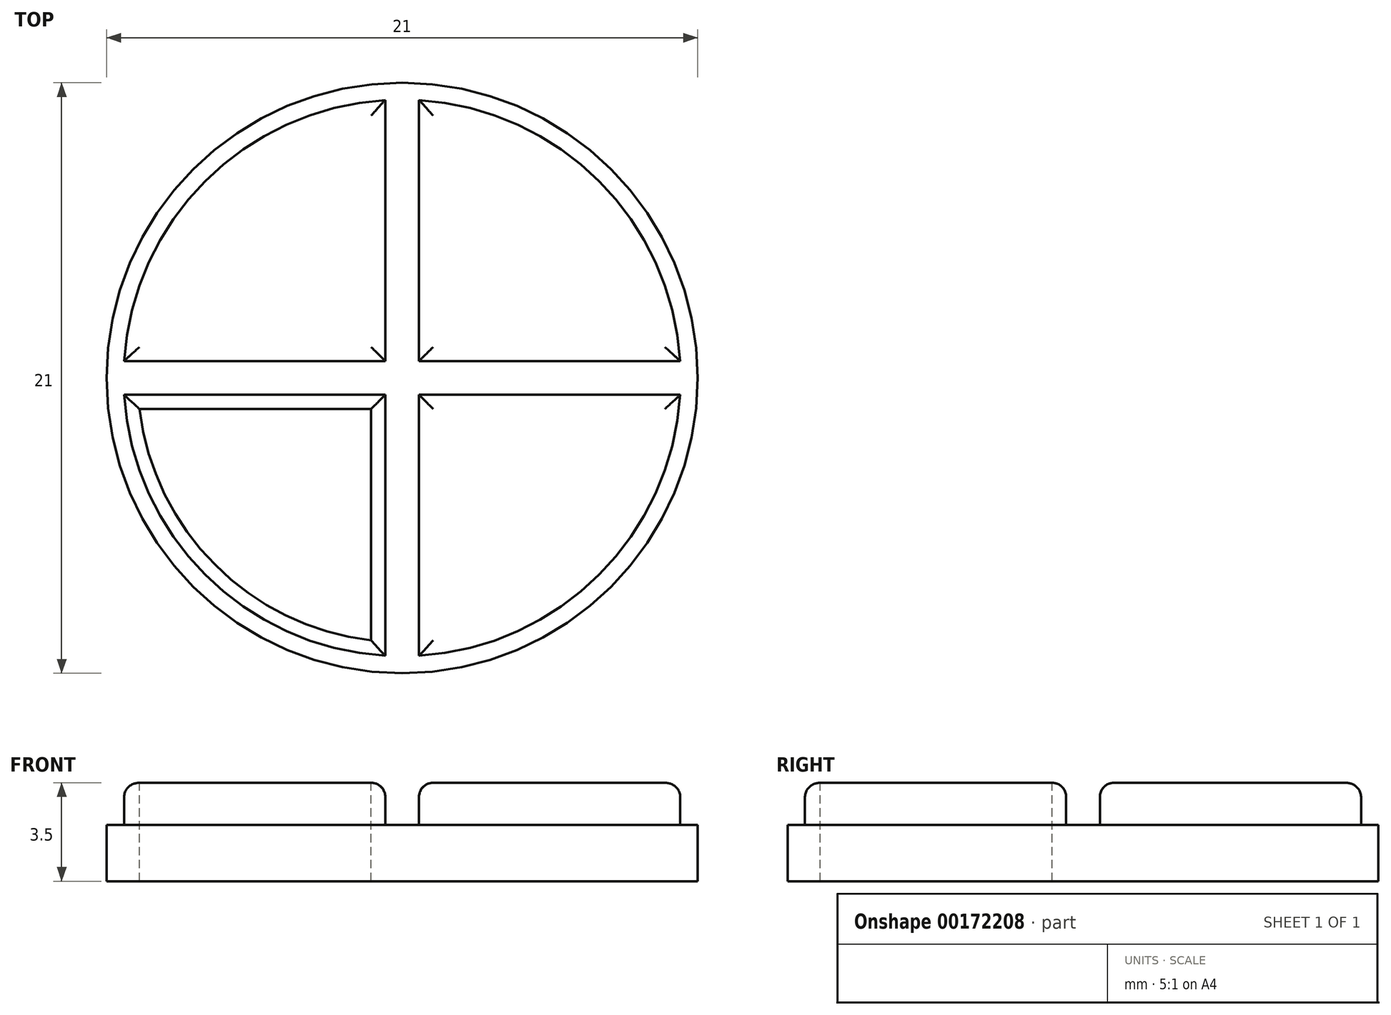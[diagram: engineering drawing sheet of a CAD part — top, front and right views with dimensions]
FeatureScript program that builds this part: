
annotation { "Feature Type Name" : "Feature", "Feature Type Description" : "" }
export const myFeature = defineFeature(function(context is Context, id is Id, definition is map)
    precondition{}
    {
        {
            var Q0;
            Q0=qCreatedBy(makeId("Top.planeOp"),FACE);
            var sketch = newSketch(context, id + "F0", { "sketchPlane" : qUnion([Q0])});
            skCircle(sketch, "E0", {"center": v(0, 0) * mm, "radius": 10.5 * mm});
            skSolve(sketch);
        }
        {
            var Q0;
            Q0=qSketchRegion(id+"F0",true);
            extrude(context, id + "F1", {"entities" : qUnion([Q0]), "depth" : 2 * mm});
        }
        {
            var Q0;
            Q0=makeQuery(id+"F1.opExtrude","CAP_FACE",FACE,{"disambiguationData":[OSD([sQuery(id+"F0.wireOp",EDGE,"E0")])],"isStart":false});
            var sketch = newSketch(context, id + "F2", { "sketchPlane" : qUnion([Q0])});
            skCircle(sketch, "E1", {"center": v(0, 0) * mm, "radius": 9.9 * mm});
            skLineSegment(sketch, "E2.bottom", {"start": v(9.88, -0.6) * mm, "end": v(-9.88, -0.6) * mm});
            skLineSegment(sketch, "E2.top", {"start": v(9.88, 0.6) * mm, "end": v(-9.88, 0.6) * mm});
            skLineSegment(sketch, "E2.left", {"start": v(9.88, -0.6) * mm, "end": v(9.88, 0.6) * mm});
            skLineSegment(sketch, "E2.right", {"start": v(-9.88, -0.6) * mm, "end": v(-9.88, 0.6) * mm});
            skLineSegment(sketch, "E3.bottom", {"start": v(0.6, -9.88) * mm, "end": v(-0.6, -9.88) * mm});
            skLineSegment(sketch, "E3.top", {"start": v(0.6, 9.88) * mm, "end": v(-0.6, 9.88) * mm});
            skLineSegment(sketch, "E3.left", {"start": v(0.6, -9.88) * mm, "end": v(0.6, 9.88) * mm});
            skLineSegment(sketch, "E3.right", {"start": v(-0.6, -9.88) * mm, "end": v(-0.6, 9.88) * mm});
            skSolve(sketch);
        }
        {
            var Q0;
            {var subQ0=sQuery(id+"F2.wireOp",EDGE,"E2.bottom");var subQ3=sQuery(id+"F2.wireOp",EDGE,"E3.right");var subQ5=makeQuery(id+"F2.imprint","INTERSECT",VERTEX,{"derivedFrom":[subQ0,subQ3]});Q0=makeQuery(id+"F2.imprint","IMPRINT",FACE,{"disambiguationData":[TD([[makeQuery(id+"F2.imprint","IMPRINT",EDGE,{"disambiguationData":[TD([[subQ5,-1.0]])],"derivedFrom":subQ0}),1.0]])]});}
            var Q1;
            {var subQ0=sQuery(id+"F2.wireOp",EDGE,"E2.top");var subQ3=sQuery(id+"F2.wireOp",EDGE,"E3.right");var subQ5=makeQuery(id+"F2.imprint","INTERSECT",VERTEX,{"derivedFrom":[subQ0,subQ3]});Q1=makeQuery(id+"F2.imprint","IMPRINT",FACE,{"disambiguationData":[TD([[makeQuery(id+"F2.imprint","IMPRINT",EDGE,{"disambiguationData":[TD([[subQ5,-1.0]])],"derivedFrom":subQ0}),-1.0]])]});}
            var Q2;
            {var subQ0=sQuery(id+"F2.wireOp",EDGE,"E2.top");var subQ3=sQuery(id+"F2.wireOp",EDGE,"E3.left");var subQ5=makeQuery(id+"F2.imprint","INTERSECT",VERTEX,{"derivedFrom":[subQ0,subQ3]});Q2=makeQuery(id+"F2.imprint","IMPRINT",FACE,{"disambiguationData":[TD([[makeQuery(id+"F2.imprint","IMPRINT",EDGE,{"disambiguationData":[TD([[subQ5,1.0]])],"derivedFrom":subQ0}),-1.0]])]});}
            var Q3;
            {var subQ0=sQuery(id+"F2.wireOp",EDGE,"E2.bottom");var subQ3=sQuery(id+"F2.wireOp",EDGE,"E3.left");var subQ5=makeQuery(id+"F2.imprint","INTERSECT",VERTEX,{"derivedFrom":[subQ0,subQ3]});Q3=makeQuery(id+"F2.imprint","IMPRINT",FACE,{"disambiguationData":[TD([[makeQuery(id+"F2.imprint","IMPRINT",EDGE,{"disambiguationData":[TD([[subQ5,1.0]])],"derivedFrom":subQ0}),1.0]])]});}
            extrude(context, id + "F3", {"entities" : qUnion([Q0, Q1, Q2, Q3]), "operationType" : NewBodyOperationType.ADD, "depth" : 1.5 * mm});
        }
        {
            var Q0;
            {var subQ0=sQuery(id+"F2.wireOp",EDGE,"E1");Q0=makeQuery(id+"F3.opExtrude","CAP_EDGE",EDGE,{"disambiguationData":[OSD([subQ0]),TDD([makeQuery(id+"F2.imprint","IMPRINT",EDGE,{"disambiguationData":[TD([[makeQuery(id+"F2.imprint","INTERSECT",VERTEX,{"derivedFrom":[subQ0,sQuery(id+"F2.wireOp",EDGE,"E2.bottom"),sQuery(id+"F2.wireOp",EDGE,"E2.right")]}),-1.0]])],"derivedFrom":subQ0})])],"isStart":false});}
            var Q1;
            {var subQ0=sQuery(id+"F2.wireOp",EDGE,"E3.right");Q1=makeQuery(id+"F3.opExtrude","CAP_EDGE",EDGE,{"disambiguationData":[OSD([subQ0]),TDD([makeQuery(id+"F2.imprint","IMPRINT",EDGE,{"disambiguationData":[TD([[makeQuery(id+"F2.imprint","INTERSECT",VERTEX,{"derivedFrom":[sQuery(id+"F2.wireOp",EDGE,"E2.bottom"),subQ0]}),1.0]])],"derivedFrom":subQ0})])],"isStart":false});}
            var Q2;
            {var subQ0=sQuery(id+"F2.wireOp",EDGE,"E2.bottom");Q2=makeQuery(id+"F3.opExtrude","CAP_EDGE",EDGE,{"disambiguationData":[OSD([subQ0]),TDD([makeQuery(id+"F2.imprint","IMPRINT",EDGE,{"disambiguationData":[TD([[makeQuery(id+"F2.imprint","INTERSECT",VERTEX,{"derivedFrom":[subQ0,sQuery(id+"F2.wireOp",EDGE,"E3.right")]}),-1.0]])],"derivedFrom":subQ0})])],"isStart":false});}
            var Q3;
            {var subQ0=sQuery(id+"F2.wireOp",EDGE,"E2.top");Q3=makeQuery(id+"F3.opExtrude","CAP_EDGE",EDGE,{"disambiguationData":[OSD([subQ0]),TDD([makeQuery(id+"F2.imprint","IMPRINT",EDGE,{"disambiguationData":[TD([[makeQuery(id+"F2.imprint","INTERSECT",VERTEX,{"derivedFrom":[subQ0,sQuery(id+"F2.wireOp",EDGE,"E3.right")]}),-1.0]])],"derivedFrom":subQ0})])],"isStart":false});}
            var Q4;
            {var subQ0=sQuery(id+"F2.wireOp",EDGE,"E3.right");Q4=makeQuery(id+"F3.opExtrude","CAP_EDGE",EDGE,{"disambiguationData":[OSD([subQ0]),TDD([makeQuery(id+"F2.imprint","IMPRINT",EDGE,{"disambiguationData":[TD([[makeQuery(id+"F2.imprint","INTERSECT",VERTEX,{"derivedFrom":[sQuery(id+"F2.wireOp",EDGE,"E2.top"),subQ0]}),-1.0]])],"derivedFrom":subQ0})])],"isStart":false});}
            var Q5;
            {var subQ0=sQuery(id+"F2.wireOp",EDGE,"E2.top");Q5=makeQuery(id+"F3.opExtrude","CAP_EDGE",EDGE,{"disambiguationData":[OSD([subQ0]),TDD([makeQuery(id+"F2.imprint","IMPRINT",EDGE,{"disambiguationData":[TD([[makeQuery(id+"F2.imprint","INTERSECT",VERTEX,{"derivedFrom":[subQ0,sQuery(id+"F2.wireOp",EDGE,"E3.left")]}),1.0]])],"derivedFrom":subQ0})])],"isStart":false});}
            var Q6;
            {var subQ0=sQuery(id+"F2.wireOp",EDGE,"E3.left");Q6=makeQuery(id+"F3.opExtrude","CAP_EDGE",EDGE,{"disambiguationData":[OSD([subQ0]),TDD([makeQuery(id+"F2.imprint","IMPRINT",EDGE,{"disambiguationData":[TD([[makeQuery(id+"F2.imprint","INTERSECT",VERTEX,{"derivedFrom":[sQuery(id+"F2.wireOp",EDGE,"E2.top"),subQ0]}),-1.0]])],"derivedFrom":subQ0})])],"isStart":false});}
            var Q7;
            {var subQ0=sQuery(id+"F2.wireOp",EDGE,"E2.bottom");Q7=makeQuery(id+"F3.opExtrude","CAP_EDGE",EDGE,{"disambiguationData":[OSD([subQ0]),TDD([makeQuery(id+"F2.imprint","IMPRINT",EDGE,{"disambiguationData":[TD([[makeQuery(id+"F2.imprint","INTERSECT",VERTEX,{"derivedFrom":[subQ0,sQuery(id+"F2.wireOp",EDGE,"E3.left")]}),1.0]])],"derivedFrom":subQ0})])],"isStart":false});}
            var Q8;
            {var subQ0=sQuery(id+"F2.wireOp",EDGE,"E3.left");Q8=makeQuery(id+"F3.opExtrude","CAP_EDGE",EDGE,{"disambiguationData":[OSD([subQ0]),TDD([makeQuery(id+"F2.imprint","IMPRINT",EDGE,{"disambiguationData":[TD([[makeQuery(id+"F2.imprint","INTERSECT",VERTEX,{"derivedFrom":[sQuery(id+"F2.wireOp",EDGE,"E2.bottom"),subQ0]}),1.0]])],"derivedFrom":subQ0})])],"isStart":false});}
            var Q9;
            {var subQ0=sQuery(id+"F2.wireOp",EDGE,"E1");Q9=makeQuery(id+"F3.opExtrude","CAP_EDGE",EDGE,{"disambiguationData":[OSD([subQ0]),TDD([makeQuery(id+"F2.imprint","IMPRINT",EDGE,{"disambiguationData":[TD([[makeQuery(id+"F2.imprint","INTERSECT",VERTEX,{"derivedFrom":[subQ0,sQuery(id+"F2.wireOp",EDGE,"E2.bottom"),sQuery(id+"F2.wireOp",EDGE,"E2.left")]}),1.0]])],"derivedFrom":subQ0})])],"isStart":false});}
            var Q10;
            {var subQ0=sQuery(id+"F2.wireOp",EDGE,"E1");Q10=makeQuery(id+"F3.opExtrude","CAP_EDGE",EDGE,{"disambiguationData":[OSD([subQ0]),TDD([makeQuery(id+"F2.imprint","IMPRINT",EDGE,{"disambiguationData":[TD([[makeQuery(id+"F2.imprint","INTERSECT",VERTEX,{"derivedFrom":[subQ0,sQuery(id+"F2.wireOp",EDGE,"E2.top"),sQuery(id+"F2.wireOp",EDGE,"E2.left")]}),-1.0]])],"derivedFrom":subQ0})])],"isStart":false});}
            var Q11;
            {var subQ0=sQuery(id+"F2.wireOp",EDGE,"E1");Q11=makeQuery(id+"F3.opExtrude","CAP_EDGE",EDGE,{"disambiguationData":[OSD([subQ0]),TDD([makeQuery(id+"F2.imprint","IMPRINT",EDGE,{"disambiguationData":[TD([[makeQuery(id+"F2.imprint","INTERSECT",VERTEX,{"derivedFrom":[subQ0,sQuery(id+"F2.wireOp",EDGE,"E2.top"),sQuery(id+"F2.wireOp",EDGE,"E2.right")]}),1.0]])],"derivedFrom":subQ0})])],"isStart":false});}
            fillet(context, id + "F4", {"entities" : qUnion([Q0, Q1, Q2, Q3, Q4, Q5, Q6, Q7, Q8, Q9, Q10, Q11]), "radius" : 0.5 * mm, "tangentPropagation" : true, "allowEdgeOverflow" : false});
        }
        {
            var Q0;
            Q0=makeQuery(id+"F3.opExtrude","CAP_FACE",FACE,{"disambiguationData":[OSD([sQuery(id+"F2.wireOp",EDGE,"E1"),sQuery(id+"F2.wireOp",EDGE,"E2.bottom"),sQuery(id+"F2.wireOp",EDGE,"E3.right")])],"isStart":false});
            extrude(context, id + "F5", {"entities" : qUnion([Q0]), "operationType" : NewBodyOperationType.REMOVE, "oppositeDirection" : true, "depth" : 25 * mm});
        }
    });
